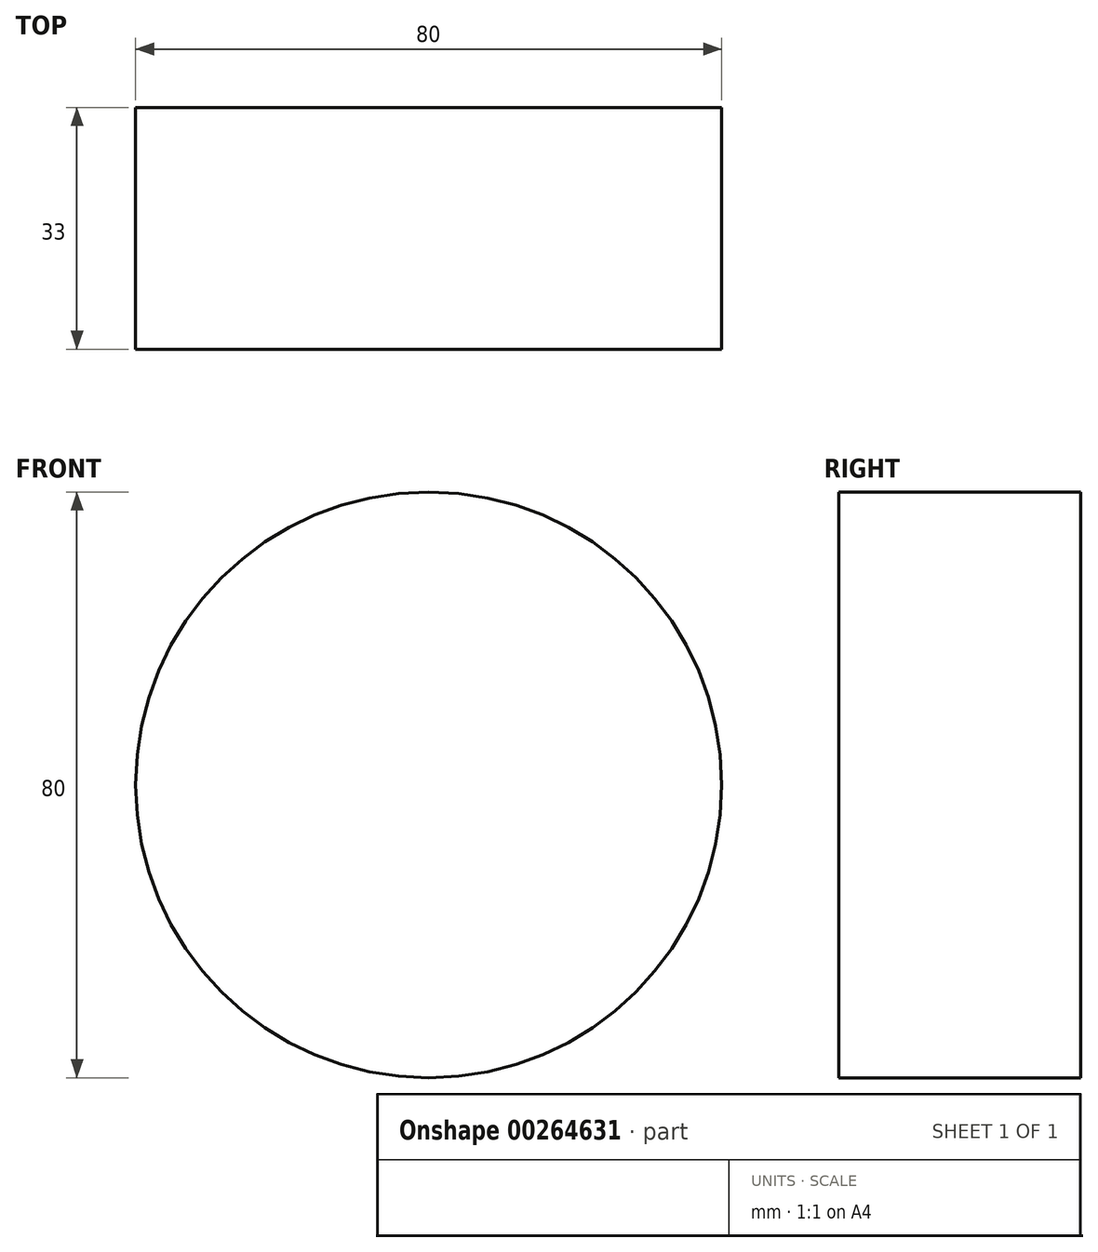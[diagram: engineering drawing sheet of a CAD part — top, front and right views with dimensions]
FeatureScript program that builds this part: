
annotation { "Feature Type Name" : "Feature", "Feature Type Description" : "" }
export const myFeature = defineFeature(function(context is Context, id is Id, definition is map)
    precondition{}
    {
        {
            var Q0;
            Q0=qCreatedBy(makeId("Front.planeOp"),FACE);
            var sketch = newSketch(context, id + "F0", { "sketchPlane" : qUnion([Q0])});
            skCircle(sketch, "E0", {"center": v(0, 0) * mm, "radius": 40 * mm});
            skSolve(sketch);
        }
        {
            var Q0;
            Q0 = qSketchRegion(id + "F0", true);
            extrude(context, id + "F1", {"entities" : qUnion([Q0]), "depth" : 33 * mm});
        }
    });
